# Revit family: Electronics_Desk-Stations_Biamp_Vocia_Desktop-Paging-Station_DS-4__
name_source: partatom
category: Communication Devices
units: mm (PartAtom-declared; Revit-internal decimal feet)

## family parameters
Cut with Voids When Loaded = No
Host = Face
Maintain Annotation Orientation = No
OmniClass Number = 23.85.10.11.14
OmniClass Title = Audio Equipment
Part Type = Normal
Room Calculation Point = No
Round Connector Dimension = Use Diameter
Shared = No

## types (1)
- DS-4
    12V DC Out = 50mA
    A/D Converters = 24-bit
    Altitude = 0-10,000 ft (0-3000 m) MSL
    Apparent Load = 0 VA
    Balanced Line In = -10dB Nominal
    Compliance = CE marked (Europe), UL and C-UL listed (USA and Canada), RoHS Directive (Europe)
    Connector Description = 802.3af (PoE) Class 2
    Default Elevation = 4' - 0"
    Depth = 0' - 7 13/32"
    Description = Vocia® DS-4 Desktop Paging Station
    Effective Input Headroom = 30dB
    Frequency Response = (100Hz ~ 20kHz): +0, -1dB
    Gain = Adjustable in 1dB steps over a 30dB range
    Height = 0' - 2 3/32"
    Housing Material = Biamp - Plastic - Black
    Humidity = 0-95% relative humidity (non-condensing)
    Input Impedance = 3 kohm
    Manufacturer = Biamp
    Max Power Consumption = 0 W
    Maximum Input = 125dB SPL
    Microphone Frequency Response = 100Hz-10kHz
    Microphone Gooseneck Length = 1' - 0 1/2"
    Microphone Pattern = Cardioid
    Microphone Type = Dynamic microphone with dual transducer (monitored)
    Model = Vocia DS-4
    Network Connection = RJ45 with shielded Ethernet (CAT5, CAT5e, CAT6 or CAT7)
    Number of Poles = 1
    PTT = Switch contact between pin and ground
    Power Factor = 1
    Product Documentation Link = https://downloads.biamp.com
    Product Page URL = https://www.biamp.com
    Product data url = https://www.bimobject.com
    RS-232 = 57600 kbps
    Sample Rate = 48kHz
    System Headroom = 18dB
    THD+N = (100Hz ~ 8kHz): <0.05%
    Temperature Range = 23 - 104° F (-5 – 40° C)
    URL = https://www.biamp.com
    Voltage = 0 V
    Weight = 3.10 lbf
    Width = 0' - 9 1/2"

## geometry (parser evidence)
native form markers: Sweep x2
no freeform markers — native parametric forms only
